# Revit family: Plumbing-Urinal-Sloan-Valve-SU-7419_
name_source: partatom
category: Plumbing Fixtures
units: mm (PartAtom-declared; Revit-internal decimal feet)

## family parameters
Cut with Voids When Loaded = No
Host = Face
OmniClass Number = 23.45.05.21.11.21
OmniClass Title = Urinals
Part Type = Normal
Room Calculation Point = No
Round Connector Dimension = Use Diameter
Shared = No

## types (2) — shared parameters
Assembly Code = D2010
CW Connection = Yes
CWFU = 5
Default Elevation = 0"
Depth = 14 3/4"
Edition number = 1
Flow Rate = 8.5 gpm (32.2 Lpm)
Flush Rate = 0.125 – 1.0 gpf (0.5 – 3.8 Lpf) - Flush volume determined by the flushometer used with the fixture
HW Connection = Yes
Height = 23 1/8"
Keynote = 15410
Manufacturer = Sloan Valve
Maximum Static Pressure = 80 PSI (552 kPa)
Product Material = Sloan Valve - Vitreous China - White
Product data url = https://bimobject.com
Sanitary Drain Connection Diameter = 2"
Sanitary Drain Connector Description = Sanitary Drain Connection
URL = www.sloanvalve.com
Valve Pressure Drop = 0.00 psi
Vent Connection = Yes
WFU = 5
Waste Connection = Yes
Water Inlet Connection Description = Water Inlet Connection
Water Inlet Connection Diameter = 1"
Width = 12 5/8"
zero-valued in all types: HWFU

## per-type parameters (varying)
| type | Description | Part Number |
| SU-7419 | Vitreous China Washdown Urinal. | 1107419 |
| SU-7419-STG | Vitreous China Washdown Urinal with SloanTec® Glaze. | 1177419 |

note: column(s) folded — value = type name in every type: Model

## geometry (parser evidence)
native form markers: Sweep x4
no freeform markers — native parametric forms only
